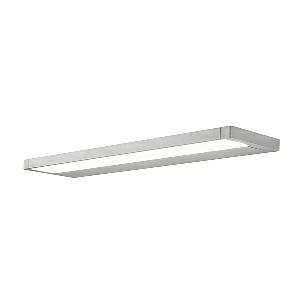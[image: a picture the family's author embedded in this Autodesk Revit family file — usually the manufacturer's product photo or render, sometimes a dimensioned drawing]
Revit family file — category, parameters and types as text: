
# Revit family: zera_wall_-_zew_3000_vtl_00812524_3407
name_source: partatom
category: Lighting Fixtures
units: mm (PartAtom-declared; Revit-internal decimal feet)

## family parameters
Cut with Voids When Loaded = No
Host = Face
Light Source = No
Part Type = Normal
Room Calculation Point = No
Round Connector Dimension = Use Diameter
Shared = No

## types (1)
- ZERA.wall - ZEW 3000/VTL (1 x LED VTL, 3150 lm, 3000-6500K)
    Apparent Load = 27 VA
    Approval mark = CE
    CIE Flux Codes = 47 78 95 33 100
    Color Rendering = 80-89
    Color Temperature = 3000-6500K
    Control Gear = Electronic ballast
    Default Elevation = 2000 mm  [stored 6.56168 ft]
    Description = ZEW 3000/VTL|Wall-mounted luminaire|light source:      |work equipment: Electronic ballast dimable digital|luminous flux: 3150 lm|light distribution: Direct/indirect|class of protection: I|technology: Continuously dimmable|mains lead: Connector 5 pin|glare control: Diffusor|special features: Asymmetric radiation, Biodynamic light VTL, DALI Load 2x, DIN EN 60598-2-25, External control device required for DALI Device Type 6, Suitable as emergency lighting|
    Frequency = 50 Hz, 60 Hz
    Height = 29 mm
    Lamp = 1 x LED VTL
    Lamp Light Flux = 3150 lm
    Lamp count = 1
    Length = 550 mm
    Luminous efficacy = 117 lm/W
    Manufacturer = Waldmann
    ModVariant = No
    Model = 00812524
    Mounting Place = Wall
    Mounting Type = Surface mounted
    Number of Poles = 1
    OnlyDefault = Yes
    Power Factor = 1
    Product Name = ZERA.wall - ZEW 3000/VTL
    Product group = Wall mounted Luminaire
    ProductGroupID = 20
    Protection Class = Protection class I
    Protection Degree = IP 20
    RLX_Detail_Level = 1
    RLX_Emergency_Light_Flux = 0 lm
    RLX_Emergency_Type = 0
    RLX_Emergency_Type_DB = No
    RlxData = <blob elided: 34785 chars, md5=bb1a8770>
    Socket = socket
    Standby Power = 0 W
    System Light Flux = 3150 lm
    System Power = 27 W
    Type Comments = Product without accessories
    Type Image = zera_bath_20_w.jpg
    URL = http://relux.com
    VarID = ---
    Voltage = 230 V
    Voltage Range = 220-240 V
    Weight = 0.00 kg
    Width = 142 mm

note: [stored X ft] marks values corroborated as IEEE doubles in the binary element streams (Revit-internal decimal feet)

## geometry (parser evidence)
native form markers: Blend x4, Sweep x10
no freeform markers — native parametric forms only
